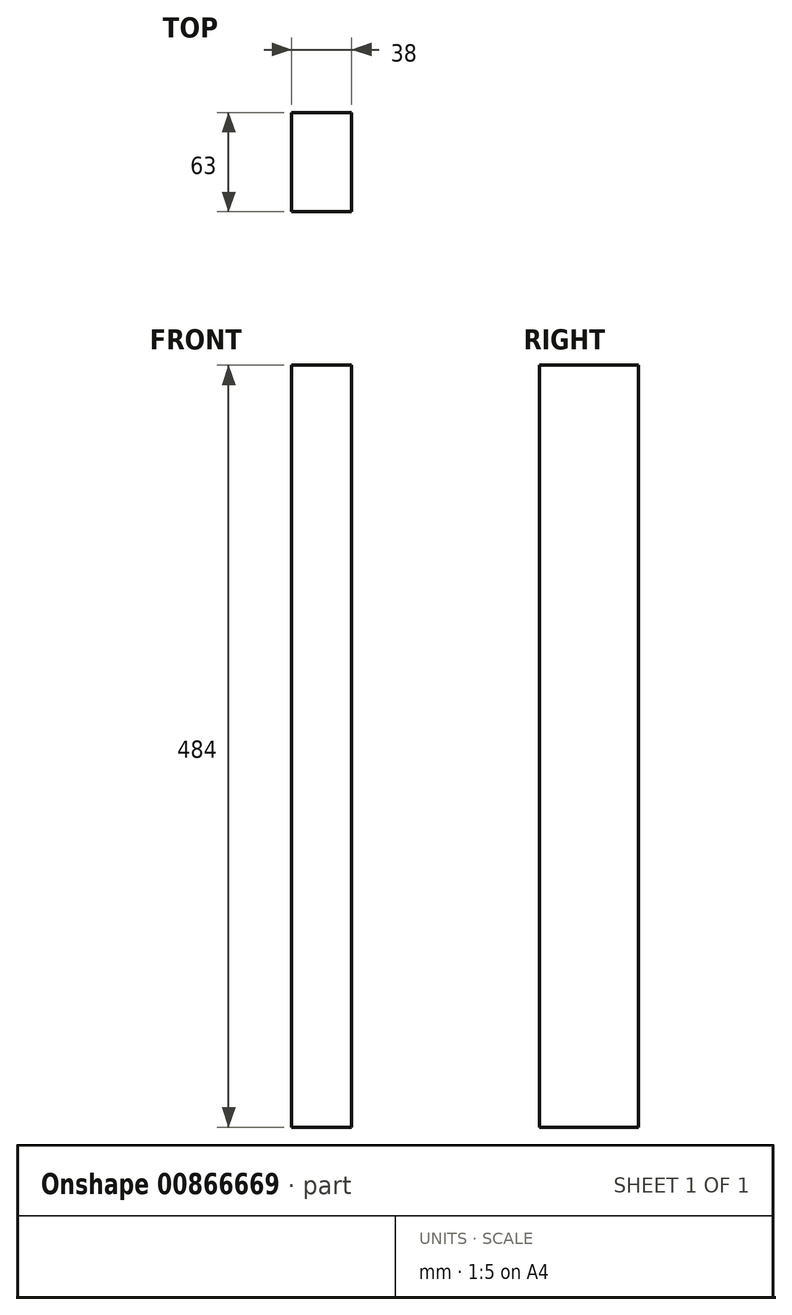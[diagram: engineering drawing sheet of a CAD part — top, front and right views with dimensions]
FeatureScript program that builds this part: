
annotation { "Feature Type Name" : "Feature", "Feature Type Description" : "" }
export const myFeature = defineFeature(function(context is Context, id is Id, definition is map)
    precondition{}
    {
        {
            var Q0;
            Q0=qCreatedBy(makeId("Top.planeOp"),FACE);
            var sketch = newSketch(context, id + "F0", { "sketchPlane" : qUnion([Q0])});
            skLineSegment(sketch, "E0.bottom", {"start": v(-19, 31.5) * mm, "end": v(19, 31.5) * mm});
            skLineSegment(sketch, "E0.top", {"start": v(-19, -31.5) * mm, "end": v(19, -31.5) * mm});
            skLineSegment(sketch, "E0.left", {"start": v(-19, 31.5) * mm, "end": v(-19, -31.5) * mm});
            skLineSegment(sketch, "E0.right", {"start": v(19, 31.5) * mm, "end": v(19, -31.5) * mm});
            skPoint(sketch, "E0.middle", {"position": v(0, 0) * mm});
            skSolve(sketch);
        }
        {
            var Q0;
            Q0 = qSketchRegion(id + "F0", true);
            extrude(context, id + "F1", {"entities" : qUnion([Q0]), "depth" : 484 * mm, "offsetDistance" : 25 * mm});
        }
    });
